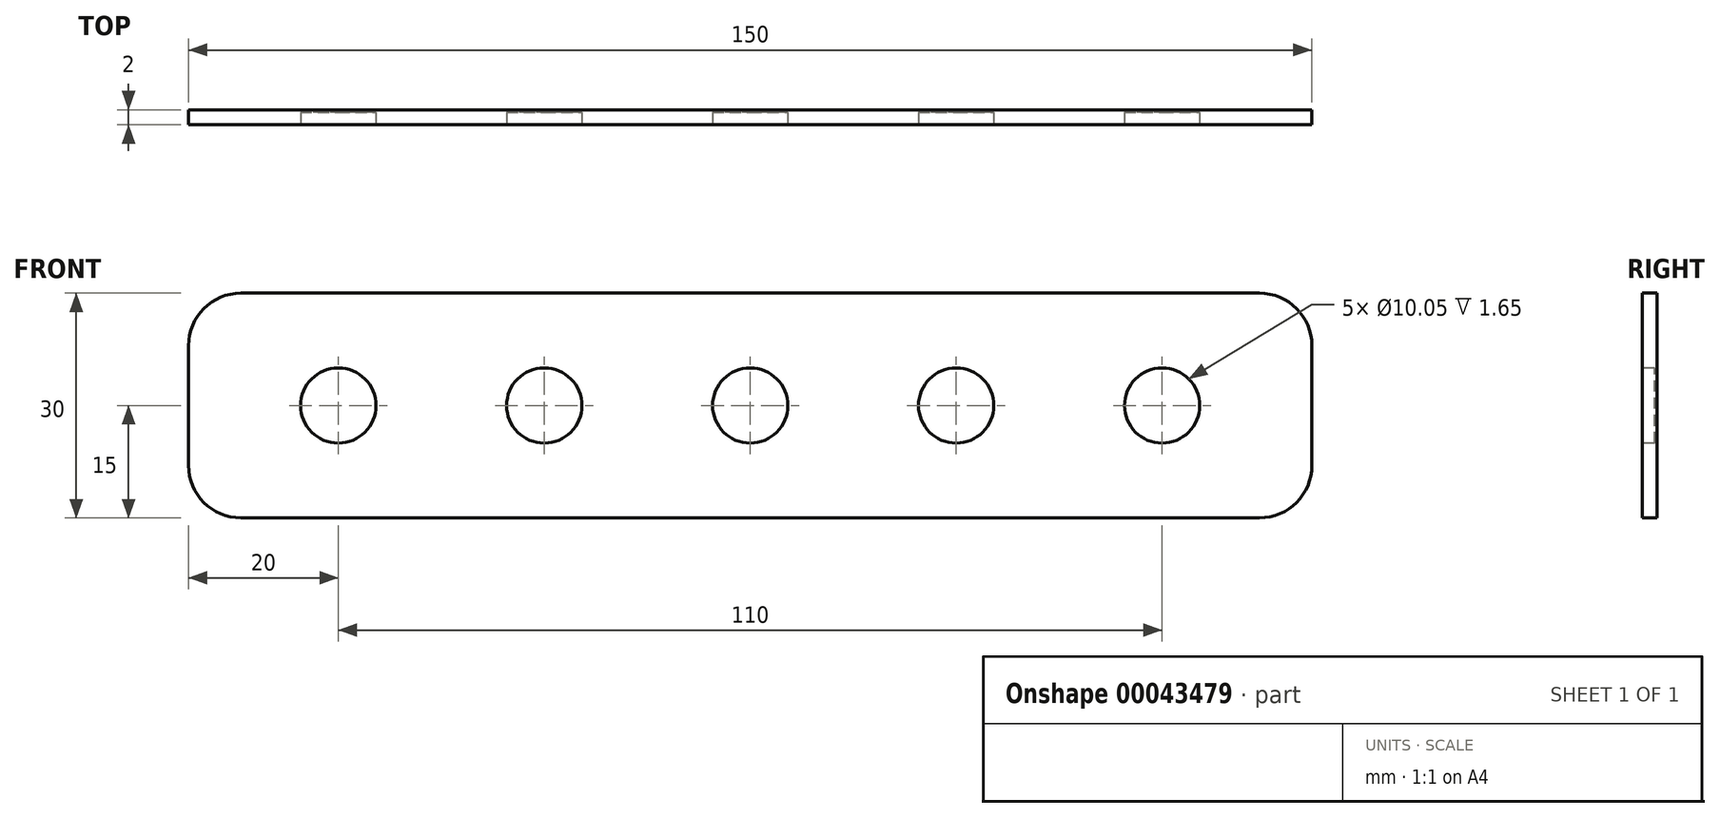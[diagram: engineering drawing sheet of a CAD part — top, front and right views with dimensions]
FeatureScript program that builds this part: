
annotation { "Feature Type Name" : "Feature", "Feature Type Description" : "" }
export const myFeature = defineFeature(function(context is Context, id is Id, definition is map)
    precondition{}
    {
        {
            var Q0;
            Q0=qCreatedBy(makeId("Front.planeOp"),FACE);
            var sketch = newSketch(context, id + "F0", { "sketchPlane" : qUnion([Q0])});
            skLineSegment(sketch, "E0.bottom", {"start": v(7, 0) * mm, "end": v(143, 0) * mm});
            skLineSegment(sketch, "E0.top", {"start": v(7, 30) * mm, "end": v(143, 30) * mm});
            skLineSegment(sketch, "E0.left", {"start": v(0, 7) * mm, "end": v(0, 23) * mm});
            skLineSegment(sketch, "E0.right", {"start": v(150, 7) * mm, "end": v(150, 23) * mm});
            skPoint(sketch, "E1.visualSharp", {"position": v(0, 30) * mm});
            skArc(sketch, "E1.filletArc", {"start": v(7, 30) * mm, "mid": v(2.05, 27.95) * mm, "end": v(0, 23) * mm});
            skPoint(sketch, "E2.visualSharp", {"position": v(0, 0) * mm});
            skArc(sketch, "E2.filletArc", {"start": v(0, 7) * mm, "mid": v(2.05, 2.05) * mm, "end": v(7, 0) * mm});
            skPoint(sketch, "E3.visualSharp", {"position": v(150, 30) * mm});
            skArc(sketch, "E3.filletArc", {"start": v(150, 23) * mm, "mid": v(147.95, 27.95) * mm, "end": v(143, 30) * mm});
            skPoint(sketch, "E4.visualSharp", {"position": v(150, 0) * mm});
            skArc(sketch, "E4.filletArc", {"start": v(143, 0) * mm, "mid": v(147.95, 2.05) * mm, "end": v(150, 7) * mm});
            skSolve(sketch);
        }
        {
            var Q0;
            Q0=makeQuery(id+"F0.imprint","IMPRINT",FACE,{"disambiguationData":[TD([[makeQuery(id+"F0.imprint","IMPRINT",EDGE,{"derivedFrom":sQuery(id+"F0.wireOp",EDGE,"E0.bottom")}),1.0]])]});
            extrude(context, id + "F1", {"entities" : qUnion([Q0]), "depth" : 2 * mm});
        }
        {
            var Q0;
            Q0=makeQuery(id+"F1.opExtrude","CAP_FACE",FACE,{"disambiguationData":[OSD([sQuery(id+"F0.wireOp",EDGE,"E0.bottom"),sQuery(id+"F0.wireOp",EDGE,"E0.top"),sQuery(id+"F0.wireOp",EDGE,"E0.left"),sQuery(id+"F0.wireOp",EDGE,"E0.right"),sQuery(id+"F0.wireOp",EDGE,"E1.filletArc"),sQuery(id+"F0.wireOp",EDGE,"E2.filletArc"),sQuery(id+"F0.wireOp",EDGE,"E3.filletArc"),sQuery(id+"F0.wireOp",EDGE,"E4.filletArc")])],"isStart":false});
            var sketch = newSketch(context, id + "F2", { "sketchPlane" : qUnion([Q0])});
            skCircle(sketch, "E5", {"center": v(20, 15) * mm, "radius": 5.03 * mm});
            skPoint(sketch, "E5.centerSnap0", {"position": v(0, 15) * mm});
            skCircle(sketch, "E6", {"center": v(47.5, 15) * mm, "radius": 5.03 * mm});
            skCircle(sketch, "E7", {"center": v(75, 15) * mm, "radius": 5.03 * mm});
            skCircle(sketch, "E8", {"center": v(102.5, 15) * mm, "radius": 5.03 * mm});
            skCircle(sketch, "E9", {"center": v(130, 15) * mm, "radius": 5.03 * mm});
            skSolve(sketch);
        }
        {
            var Q0;
            Q0 = qSketchRegion(id + "F2", true);
            extrude(context, id + "F3", {"entities" : qUnion([Q0]), "operationType" : NewBodyOperationType.REMOVE, "oppositeDirection" : true, "depth" : 1.65 * mm});
        }
    });
